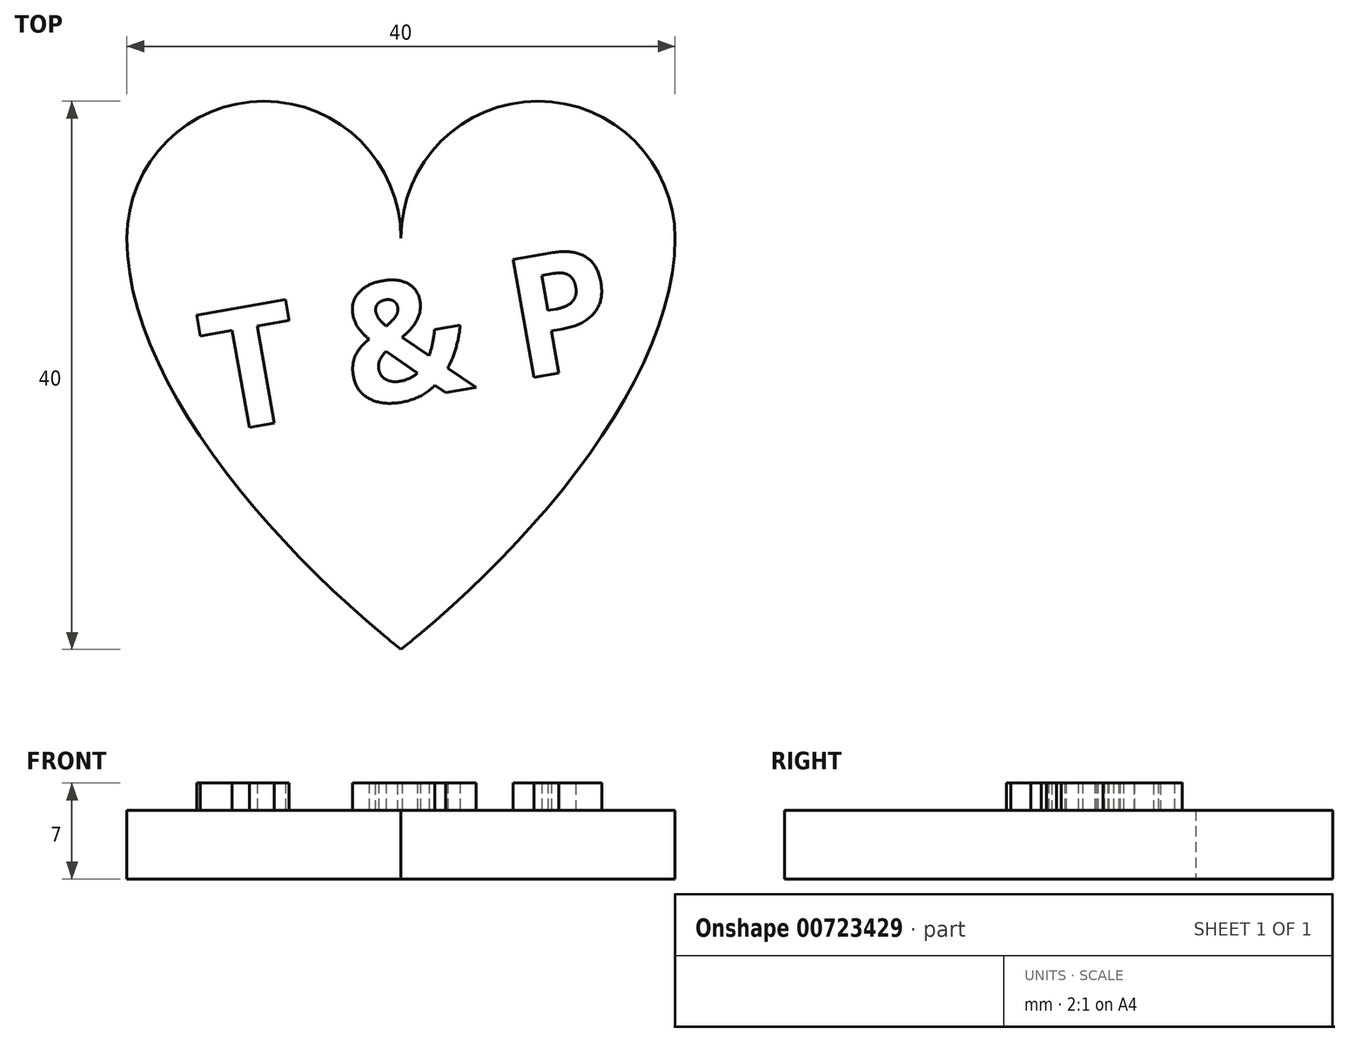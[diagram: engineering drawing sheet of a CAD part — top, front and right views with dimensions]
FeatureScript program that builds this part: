
annotation { "Feature Type Name" : "Feature", "Feature Type Description" : "" }
export const myFeature = defineFeature(function(context is Context, id is Id, definition is map)
    precondition{}
    {
        {
            var Q0;
            Q0=qCreatedBy(makeId("Top.planeOp"),FACE);
            var sketch = newSketch(context, id + "F0", { "sketchPlane" : qUnion([Q0])});
            skLineSegment(sketch, "E0", {"start": v(0, 0) * mm, "end": v(10, 0) * mm});
            skLineSegment(sketch, "E1", {"start": v(0, 0) * mm, "end": v(-10, 0) * mm});
            skCircle(sketch, "E2", {"center": v(10, 0) * mm, "radius": 10 * mm});
            skCircle(sketch, "E3", {"center": v(-10, 0) * mm, "radius": 10 * mm});
            skLineSegment(sketch, "E4", {"start": v(0, 0) * mm, "end": v(0, -30) * mm});
            skPoint(sketch, "E5.visualSharp", {"position": v(0, -30) * mm});
            skLineSegment(sketch, "E6", {"start": v(-10, 0) * mm, "end": v(-10, 5) * mm});
            skLineSegment(sketch, "E7", {"start": v(10, 0) * mm, "end": v(10, 5) * mm});
            skLineSegment(sketch, "E8", {"start": v(-20, 0) * mm, "end": v(-20, -10) * mm});
            skLineSegment(sketch, "E9", {"start": v(20, 0) * mm, "end": v(20, -10) * mm});
            skFitSpline(sketch, "E10", {"points": [v(-20, 0) * mm, v(0, -30) * mm], "startDerivative": vector(0, -30) * mm, "endDerivative": vector(30, -24) * mm});
            skFitSpline(sketch, "E11", {"points": [v(0, -30) * mm, v(20, 0) * mm], "startDerivative": vector(30, 24) * mm, "endDerivative": vector(0, 30) * mm});
            skLineSegment(sketch, "E12", {"start": v(0, -30) * mm, "end": v(0, -22) * mm});
            skArc(sketch, "E13.filletArc", {"start": v(-1.28, -28.95) * mm, "mid": v(0, -29.42) * mm, "end": v(1.28, -28.95) * mm});
            skSolve(sketch);
        }
        {
            var Q0;
            Q0=qCreatedBy(makeId("Top.planeOp"),FACE);
            var sketch = newSketch(context, id + "F1", { "sketchPlane" : qUnion([Q0])});
            skText(sketch, "E14", { "text": "T & P", "fontName": "OpenSans-Bold.ttf"});
            skLineSegment(sketch, "E15", {"start": v(-24.1, -16.72) * mm, "end": v(-13.96, -16.72) * mm});
            const initialGuessF1  = {"E14": [-0.01364, -0.01426, 0.9848, 0.17365, 0.0088]};
            skSetInitialGuess(sketch, initialGuessF1);
            skSolve(sketch);
        }
        {
            var Q0;
            Q0 = qSketchRegion(id + "F0", true);
            extrude(context, id + "F2", {"entities" : qUnion([Q0]), "depth" : 5 * mm, "offsetDistance" : 25 * mm});
        }
        {
            var Q0;
            Q0 = qSketchRegion(id + "F1", true);
            extrude(context, id + "F3", {"entities" : qUnion([Q0]), "operationType" : NewBodyOperationType.ADD, "depth" : 7 * mm, "offsetDistance" : 25 * mm});
        }
    });
